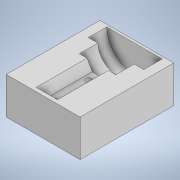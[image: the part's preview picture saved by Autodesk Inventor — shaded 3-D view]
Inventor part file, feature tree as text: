
AUTODESK INVENTOR PART (.ipt)
format: ipt  version: 2022.1 (Build 261234000, 234)  size: 884,736 bytes
history: native  units: in
note: dims shown in document units (in); Inventor stores cm internally (conversion verified against a paired STEP export)
features: extrude x4, sketch x4, boolean_combine x1, other x1
ambient origin geometry x8: Origin, YZ Plane, XZ Plane, XY Plane, X Axis, Y Axis, Z Axis, Center Point
bodies: Solid6 (feature_tree), Solid8 (feature_tree), Solid1 (feature_tree)
feature tree (10):
  boolean_combine  "Combine2"
  extrude  "Extrusion6"  Depth=0.1in TaperAngle=0.0deg
  extrude  "Extrusion7"  Depth=0.1in
  extrude  "Extrusion8"  [1 undecoded]
  extrude  "Extrusion9"  [1 undecoded]
  sketch  "Sketch9"  dims[d28=0.0in d29=0.0in d30=0.1in d31=0.0in]
  sketch  "Sketch10"  dims[d32=0.0in d33=0.0in d34=0.1in]
  sketch  "Sketch11"  dims[d35=0.0in d36=0.0in]
  sketch  "Sketch12"
  other  "Solid1:1"
note: 2 required parameter values undecoded (feature->parameter linkage not recoverable at this tier; creation-order binding heuristic only, values carry confidence <= 0.55)
